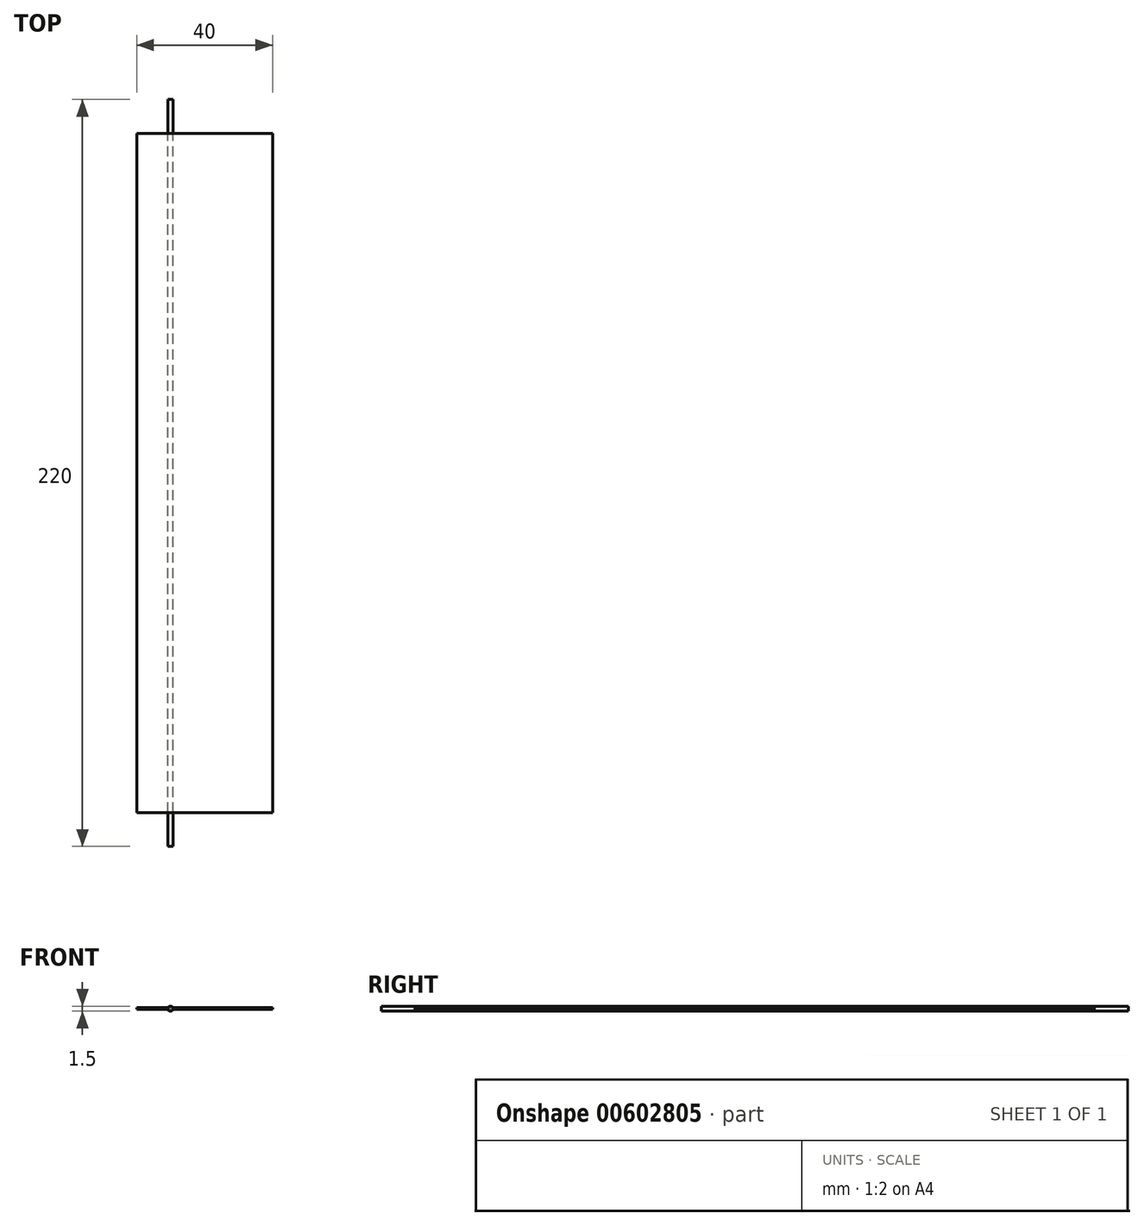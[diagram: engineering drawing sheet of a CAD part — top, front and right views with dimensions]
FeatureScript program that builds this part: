
annotation { "Feature Type Name" : "Feature", "Feature Type Description" : "" }
export const myFeature = defineFeature(function(context is Context, id is Id, definition is map)
    precondition{}
    {
        {
            var Q0;
            Q0=qCreatedBy(makeId("Front.planeOp"),FACE);
            var sketch = newSketch(context, id + "F0", { "sketchPlane" : qUnion([Q0])});
            skLineSegment(sketch, "E0.bottom", {"start": v(43.4, 30.82) * mm, "end": v(3.4, 30.82) * mm});
            skLineSegment(sketch, "E0.top", {"start": v(43.4, 30.32) * mm, "end": v(3.4, 30.32) * mm});
            skLineSegment(sketch, "E0.left", {"start": v(43.4, 30.82) * mm, "end": v(43.4, 30.32) * mm});
            skLineSegment(sketch, "E0.right", {"start": v(3.4, 30.82) * mm, "end": v(3.4, 30.32) * mm});
            skSolve(sketch);
        }
        {
            var Q0;
            Q0=makeQuery(id+"F0.imprint","IMPRINT",FACE,{"disambiguationData":[TD([[makeQuery(id+"F0.imprint","IMPRINT",EDGE,{"derivedFrom":sQuery(id+"F0.wireOp",EDGE,"E0.bottom")}),1.0]])]});
            var sketch = newSketch(context, id + "F1", { "sketchPlane" : qUnion([Q0])});
            skCircle(sketch, "E1", {"center": v(13.33, 30.48) * mm, "radius": 0.75 * mm});
            skSolve(sketch);
        }
        {
            var Q0;
            Q0 = qSketchRegion(id + "F0", true);
            extrude(context, id + "F2", {"entities" : qUnion([Q0]), "depth" : 200 * mm, "offsetDistance" : 25 * mm});
        }
        {
            var Q0;
            Q0 = qSketchRegion(id + "F1", true);
            extrude(context, id + "F3", {"entities" : qUnion([Q0]), "depth" : 210 * mm, "offsetDistance" : 25 * mm, "hasSecondDirection" : true, "secondDirectionOppositeDirection" : true, "secondDirectionDepth" : 10 * mm});
        }
    });
